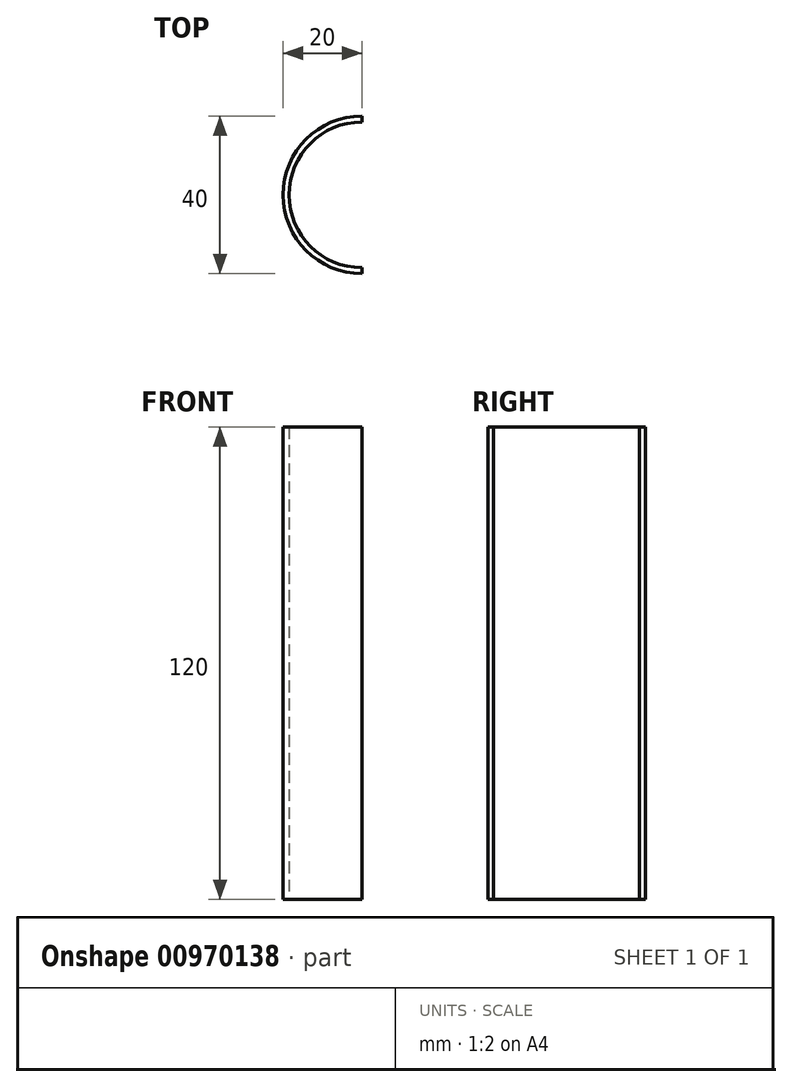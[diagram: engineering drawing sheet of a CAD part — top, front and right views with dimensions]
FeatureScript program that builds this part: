
annotation { "Feature Type Name" : "Feature", "Feature Type Description" : "" }
export const myFeature = defineFeature(function(context is Context, id is Id, definition is map)
    precondition{}
    {
        {
            var Q0;
            Q0=qCreatedBy(makeId("Front.planeOp"),FACE);
            var sketch = newSketch(context, id + "F0", { "sketchPlane" : qUnion([Q0])});
            skLineSegment(sketch, "E0", {"start": v(-18.5, 0) * mm, "end": v(-18.5, 120) * mm});
            skLineSegment(sketch, "E1", {"start": v(-18.5, 120) * mm, "end": v(-20, 120) * mm});
            skLineSegment(sketch, "E2", {"start": v(-20, 120) * mm, "end": v(-20, 0) * mm});
            skLineSegment(sketch, "E3", {"start": v(-20, 0) * mm, "end": v(-18.5, 0) * mm});
            skLineSegment(sketch, "E4", {"start": v(0, 0) * mm, "end": v(0, 47.7) * mm, "construction": true});
            skLineSegment(sketch, "E5", {"start": v(0, 47.7) * mm, "end": v(0, 33.3) * mm, "construction": true});
            skSolve(sketch);
        }
        {
            var Q0;
            Q0 = qSketchRegion(id + "F0", true);
            var Q1;
            Q1=sQuery(id+"F0.wireOp",EDGE,"E4");
            revolve(context, id + "F1", {"surfaceOperationType" : NewSurfaceOperationType.NEW, "entities" : qUnion([Q0]), "axis" : qUnion([Q1]), "revolveType" : RevolveType.SYMMETRIC, "angle" : 180 * degree});
        }
    });
